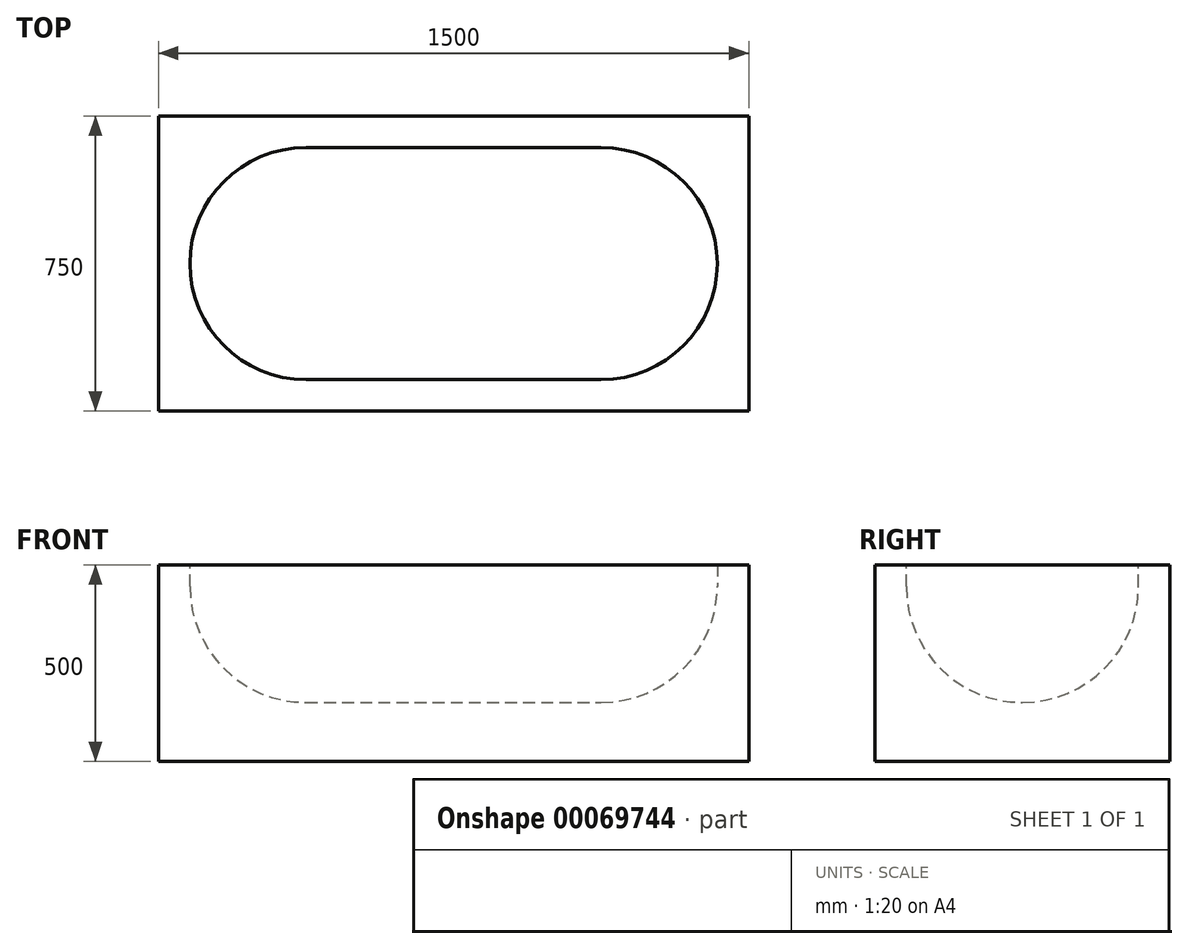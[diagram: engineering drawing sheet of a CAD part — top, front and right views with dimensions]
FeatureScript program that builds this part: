
annotation { "Feature Type Name" : "Feature", "Feature Type Description" : "" }
export const myFeature = defineFeature(function(context is Context, id is Id, definition is map)
    precondition{}
    {
        {
            var Q0;
            Q0=qCreatedBy(makeId("Top.planeOp"),FACE);
            var sketch = newSketch(context, id + "F0", { "sketchPlane" : qUnion([Q0])});
            skLineSegment(sketch, "E0.rect.bottom", {"start": v(750, -375) * mm, "end": v(-750, -375) * mm});
            skLineSegment(sketch, "E0.rect.top", {"start": v(750, 375) * mm, "end": v(-750, 375) * mm});
            skLineSegment(sketch, "E0.rect.left", {"start": v(750, -375) * mm, "end": v(750, 375) * mm});
            skLineSegment(sketch, "E0.rect.right", {"start": v(-750, -375) * mm, "end": v(-750, 375) * mm});
            skPoint(sketch, "E0.rect.middle", {"position": v(0, 0) * mm});
            skSolve(sketch);
        }
        {
            var Q0;
            Q0=makeQuery(id+"F0.imprint","IMPRINT",FACE,{"disambiguationData":[TD([[makeQuery(id+"F0.imprint","IMPRINT",EDGE,{"derivedFrom":sQuery(id+"F0.wireOp",EDGE,"E0.rect.bottom")}),-1.0]])]});
            extrude(context, id + "F1", {"entities" : qUnion([Q0]), "depth" : 500 * mm});
        }
        {
            var Q0;
            Q0=makeQuery(id+"F1.opExtrude","CAP_FACE",FACE,{"disambiguationData":[OSD([sQuery(id+"F0.wireOp",EDGE,"E0.rect.bottom"),sQuery(id+"F0.wireOp",EDGE,"E0.rect.top"),sQuery(id+"F0.wireOp",EDGE,"E0.rect.left"),sQuery(id+"F0.wireOp",EDGE,"E0.rect.right")])],"isStart":false});
            var sketch = newSketch(context, id + "F2", { "sketchPlane" : qUnion([Q0])});
            skLineSegment(sketch, "E1.0", {"start": v(670, 295) * mm, "end": v(-670, 295) * mm});
            skLineSegment(sketch, "E1.1", {"start": v(670, -295) * mm, "end": v(670, 295) * mm});
            skLineSegment(sketch, "E1.2", {"start": v(670, -295) * mm, "end": v(-670, -295) * mm});
            skLineSegment(sketch, "E1.3", {"start": v(-670, -295) * mm, "end": v(-670, 295) * mm});
            skLineSegment(sketch, "E2.0", {"start": v(-745, -370) * mm, "end": v(745, -370) * mm});
            skLineSegment(sketch, "E2.1", {"start": v(-745, 370) * mm, "end": v(-745, -370) * mm});
            skLineSegment(sketch, "E2.2", {"start": v(745, 370) * mm, "end": v(-745, 370) * mm});
            skLineSegment(sketch, "E2.3", {"start": v(745, -370) * mm, "end": v(745, 370) * mm});
            skSolve(sketch);
        }
        {
            var Q0;
            Q0=makeQuery(id+"F2.imprint","IMPRINT",FACE,{"disambiguationData":[TD([[makeQuery(id+"F2.imprint","IMPRINT",EDGE,{"derivedFrom":sQuery(id+"F2.wireOp",EDGE,"E1.0")}),1.0]])]});
            extrude(context, id + "F3", {"entities" : qUnion([Q0]), "operationType" : NewBodyOperationType.REMOVE, "oppositeDirection" : true, "depth" : 350 * mm});
        }
        {
            var Q0;
            Q0=makeQuery(id+"F3.boolean.opBoolean","COPY",EDGE,{"derivedFrom":makeQuery(id+"F3.opExtrude","SWEPT_EDGE",EDGE,{"disambiguationData":[OSD([sQuery(id+"F2.wireOp",EDGE,"E1.0"),sQuery(id+"F2.wireOp",EDGE,"E1.3")])]})});
            var Q1;
            Q1=makeQuery(id+"F3.boolean.opBoolean","COPY",EDGE,{"derivedFrom":makeQuery(id+"F3.opExtrude","SWEPT_EDGE",EDGE,{"disambiguationData":[OSD([sQuery(id+"F2.wireOp",EDGE,"E1.2"),sQuery(id+"F2.wireOp",EDGE,"E1.3")])]})});
            var Q2;
            Q2=makeQuery(id+"F3.boolean.opBoolean","COPY",EDGE,{"derivedFrom":makeQuery(id+"F3.opExtrude","SWEPT_EDGE",EDGE,{"disambiguationData":[OSD([sQuery(id+"F2.wireOp",EDGE,"E1.0"),sQuery(id+"F2.wireOp",EDGE,"E1.1")])]})});
            var Q3;
            Q3=makeQuery(id+"F3.boolean.opBoolean","COPY",EDGE,{"derivedFrom":makeQuery(id+"F3.opExtrude","SWEPT_EDGE",EDGE,{"disambiguationData":[OSD([sQuery(id+"F2.wireOp",EDGE,"E1.1"),sQuery(id+"F2.wireOp",EDGE,"E1.2")])]})});
            fillet(context, id + "F4", {"entities" : qUnion([Q0, Q1, Q2, Q3]), "radius" : 295 * mm, "tangentPropagation" : true, "allowEdgeOverflow" : false});
        }
        {
            var Q0;
            {var subQ0=sQuery(id+"F2.wireOp",EDGE,"E1.3");var subQ1=sQuery(id+"F2.wireOp",EDGE,"E1.2");Q0=makeQuery(id+"F4.opFillet","BLEND_EDGE",EDGE,{"blendedFrom":[makeQuery(id+"F3.boolean.opBoolean","COPY",EDGE,{"derivedFrom":makeQuery(id+"F3.opExtrude","SWEPT_EDGE",EDGE,{"disambiguationData":[OSD([subQ1,subQ0])]})}),makeQuery(id+"F3.boolean.opBoolean","COPY",FACE,{"derivedFrom":makeQuery(id+"F3.opExtrude","CAP_FACE",FACE,{"disambiguationData":[OSD([sQuery(id+"F2.wireOp",EDGE,"E1.0"),sQuery(id+"F2.wireOp",EDGE,"E1.1"),subQ1,subQ0])],"isStart":false})})],"blendedInto":[makeQuery(id+"F3.boolean.opBoolean","COPY",FACE,{"derivedFrom":makeQuery(id+"F3.opExtrude","CAP_FACE",FACE,{"disambiguationData":[OSD([sQuery(id+"F2.wireOp",EDGE,"E1.0"),sQuery(id+"F2.wireOp",EDGE,"E1.1"),subQ1,subQ0])],"isStart":false})})]});}
            var Q1;
            Q1=makeQuery(id+"F3.boolean.opBoolean","COPY",EDGE,{"derivedFrom":makeQuery(id+"F3.opExtrude","CAP_EDGE",EDGE,{"disambiguationData":[OSD([sQuery(id+"F2.wireOp",EDGE,"E1.0")])],"isStart":false})});
            var Q2;
            {var subQ0=sQuery(id+"F2.wireOp",EDGE,"E1.2");var subQ1=sQuery(id+"F2.wireOp",EDGE,"E1.1");Q2=makeQuery(id+"F4.opFillet","BLEND_EDGE",EDGE,{"blendedFrom":[makeQuery(id+"F3.boolean.opBoolean","COPY",EDGE,{"derivedFrom":makeQuery(id+"F3.opExtrude","SWEPT_EDGE",EDGE,{"disambiguationData":[OSD([subQ1,subQ0])]})}),makeQuery(id+"F3.boolean.opBoolean","COPY",FACE,{"derivedFrom":makeQuery(id+"F3.opExtrude","CAP_FACE",FACE,{"disambiguationData":[OSD([sQuery(id+"F2.wireOp",EDGE,"E1.0"),subQ1,subQ0,sQuery(id+"F2.wireOp",EDGE,"E1.3")])],"isStart":false})})],"blendedInto":[makeQuery(id+"F3.boolean.opBoolean","COPY",FACE,{"derivedFrom":makeQuery(id+"F3.opExtrude","CAP_FACE",FACE,{"disambiguationData":[OSD([sQuery(id+"F2.wireOp",EDGE,"E1.0"),subQ1,subQ0,sQuery(id+"F2.wireOp",EDGE,"E1.3")])],"isStart":false})})]});}
            var Q3;
            Q3=makeQuery(id+"F3.boolean.opBoolean","COPY",EDGE,{"derivedFrom":makeQuery(id+"F3.opExtrude","CAP_EDGE",EDGE,{"disambiguationData":[OSD([sQuery(id+"F2.wireOp",EDGE,"E1.2")])],"isStart":false})});
            fillet(context, id + "F5", {"entities" : qUnion([Q0, Q1, Q2, Q3]), "radius" : 295 * mm, "tangentPropagation" : true, "allowEdgeOverflow" : false});
        }
    });
